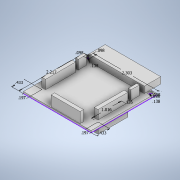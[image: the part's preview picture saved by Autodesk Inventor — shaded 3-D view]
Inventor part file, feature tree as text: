
AUTODESK INVENTOR PART (.ipt)
format: ipt  version: 2022.2 (Build 262287000, 287)  size: 182,272 bytes
history: native  units: in
note: dims shown in document units (in); Inventor stores cm internally (conversion verified against a paired STEP export)
features: extrude x6, sketch x4, other x1
ambient origin geometry x8: Origin, YZ Plane, XZ Plane, XY Plane, X Axis, Y Axis, Z Axis, Center Point
bodies: Solid1 (feature_tree)
feature tree (11):
  other  "Base Board"
  extrude  "Base Board Extrusion"  Depth=2.2165in
  extrude  "RightAngleconnectorsBase"  Depth=0.0984in
  extrude  "RightAnglePins"  Depth=0.0984in
  extrude  "Main IO"  Depth=0.0591in TaperAngle=0.0deg
  extrude  "Emulator Pins"  Depth=1.8898in
  extrude  "Power Pins"  Depth=0.1969in
  sketch  "Sketch2"  dims[d0=2.3031in d1=2.2165in]
  sketch  "Sketch4"  dims[d2=0.1382in d3=0.0984in]
  sketch  "Sketch6"  dims[d4=0.0984in d5=0.1382in d6=0.0984in]
  sketch  "Sketch7"  dims[d7=0.0984in d8=0.0591in d9=0.0in d10=1.8898in d11=0.1969in d12=0.2244in d13=0.2165in d14=0.0in d15=0.3622in d16=0.0in d19=0.126in d20=1.0157in d23=0.4331in d24=0.1969in d25=0.4331in d26=0.1969in d27=0.7283in d28=0.0in d29=0.9843in d30=0.1181in d31=0.3937in d32=0.0197in d33=0.3543in d34=0.0in d35=0.0906in d36=0.2854in d37=0.2087in d38=0.1181in d39=0.315in d40=0.0in]
